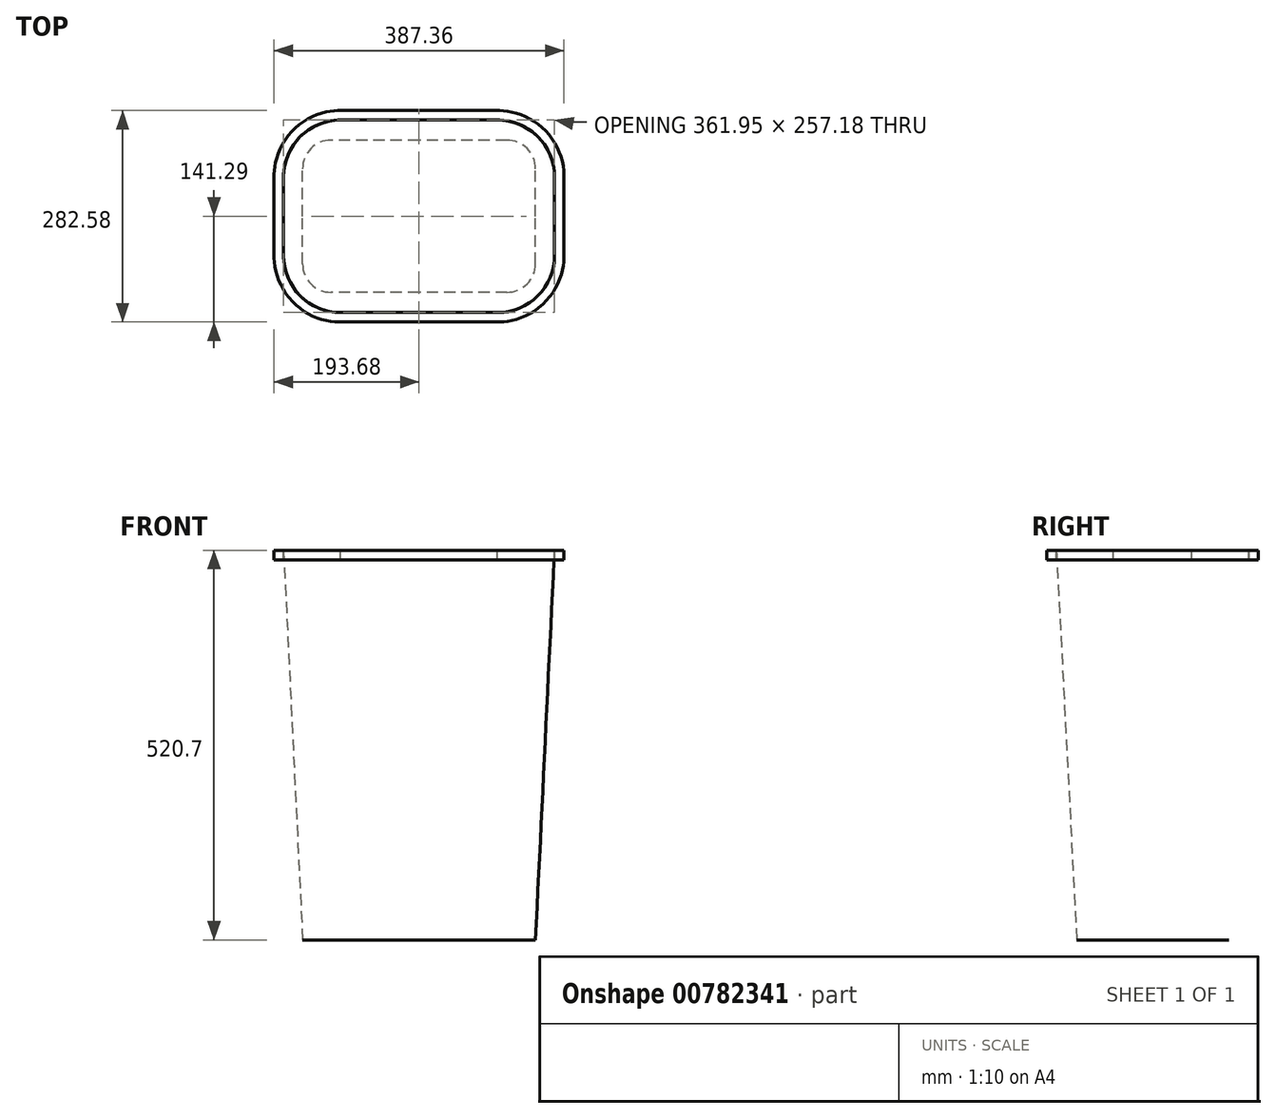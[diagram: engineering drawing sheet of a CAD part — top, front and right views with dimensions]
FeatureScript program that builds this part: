
annotation { "Feature Type Name" : "Feature", "Feature Type Description" : "" }
export const myFeature = defineFeature(function(context is Context, id is Id, definition is map)
    precondition{}
    {
        {
            var Q0;
            Q0=qCreatedBy(makeId("Top.planeOp"),FACE);
            var sketch = newSketch(context, id + "F0", { "sketchPlane" : qUnion([Q0])});
            skLineSegment(sketch, "E0.bottom", {"start": v(104.78, -128.59) * mm, "end": v(-104.78, -128.59) * mm});
            skLineSegment(sketch, "E0.top", {"start": v(104.78, 128.59) * mm, "end": v(-104.78, 128.59) * mm});
            skLineSegment(sketch, "E0.left", {"start": v(180.98, -52.39) * mm, "end": v(180.98, 52.39) * mm});
            skLineSegment(sketch, "E0.right", {"start": v(-180.97, -52.39) * mm, "end": v(-180.97, 52.39) * mm});
            skPoint(sketch, "E0.middle", {"position": v(0, 0) * mm});
            skPoint(sketch, "E1.visualSharp", {"position": v(-180.98, 128.59) * mm});
            skArc(sketch, "E1.filletArc", {"start": v(-104.78, 128.59) * mm, "mid": v(-158.66, 106.27) * mm, "end": v(-180.97, 52.39) * mm});
            skLineSegment(sketch, "E2", {"start": v(-180.97, 0) * mm, "end": v(180.97, 0) * mm, "construction": true});
            skLineSegment(sketch, "E3", {"start": v(0, 128.59) * mm, "end": v(0, -128.59) * mm});
            skArc(sketch, "E4.MirrorCS", {"start": v(-104.78, -128.59) * mm, "mid": v(-158.66, -106.27) * mm, "end": v(-180.97, -52.39) * mm});
            skLineSegment(sketch, "E5.MirrorCS", {"start": v(0, -128.59) * mm, "end": v(0, 128.59) * mm});
            skLineSegment(sketch, "E6.MirrorCS", {"start": v(0, 128.59) * mm, "end": v(0, -128.59) * mm, "construction": true});
            skArc(sketch, "E7.MirrorCS", {"start": v(104.78, 128.59) * mm, "mid": v(158.66, 106.27) * mm, "end": v(180.98, 52.39) * mm});
            skArc(sketch, "E8.MirrorCS", {"start": v(104.78, -128.59) * mm, "mid": v(158.66, -106.27) * mm, "end": v(180.98, -52.39) * mm});
            skPoint(sketch, "E9.orphan", {"position": v(-180.97, -128.59) * mm});
            skPoint(sketch, "E10.orphan", {"position": v(180.98, -128.59) * mm});
            skPoint(sketch, "E11.orphan", {"position": v(180.97, 128.59) * mm});
            skSolve(sketch);
        }
        {
            var Q0;
            {var subQ0=sQuery(id+"F0.wireOp",EDGE,"E1.filletArc");Q0=makeQuery(id+"F0.imprint","IMPRINT",FACE,{"disambiguationData":[TD([[makeQuery(id+"F0.imprint","IMPRINT",EDGE,{"derivedFrom":subQ0}),1.0]])]});}
            cPlane(context, id + "F1", {"entities" : qUnion([Q0]), "cplaneType" : CPlaneType.OFFSET, "offset" : 520.7 * mm, "oppositeDirection" : true, "width" : 152.4 * mm, "height" : 152.4 * mm});
        }
        {
            var Q0;
            Q0=qCreatedBy(id+"F1.planeOp",FACE);
            var sketch = newSketch(context, id + "F2", { "sketchPlane" : qUnion([Q0])});
            skLineSegment(sketch, "E12.0", {"start": v(-180.97, 0) * mm, "end": v(180.97, 0) * mm, "construction": true});
            skLineSegment(sketch, "E13.0", {"start": v(0, 128.59) * mm, "end": v(0, -128.59) * mm, "construction": true});
            skLineSegment(sketch, "E14.bottom", {"start": v(117.48, -101.6) * mm, "end": v(-117.48, -101.6) * mm});
            skLineSegment(sketch, "E14.top", {"start": v(117.47, 101.6) * mm, "end": v(-117.47, 101.6) * mm});
            skLineSegment(sketch, "E14.left", {"start": v(155.58, -63.5) * mm, "end": v(155.58, 63.5) * mm});
            skLineSegment(sketch, "E14.right", {"start": v(-155.57, -63.5) * mm, "end": v(-155.57, 63.5) * mm});
            skPoint(sketch, "E14.middle", {"position": v(0, 0) * mm});
            skPoint(sketch, "E15.visualSharp", {"position": v(-155.57, 101.6) * mm});
            skArc(sketch, "E15.filletArc", {"start": v(-117.48, 101.6) * mm, "mid": v(-144.42, 90.44) * mm, "end": v(-155.57, 63.5) * mm});
            skArc(sketch, "E16.MirrorCS", {"start": v(-117.47, -101.6) * mm, "mid": v(-144.42, -90.44) * mm, "end": v(-155.57, -63.5) * mm});
            skArc(sketch, "E17.MirrorCS", {"start": v(117.47, 101.6) * mm, "mid": v(144.42, 90.44) * mm, "end": v(155.58, 63.5) * mm});
            skArc(sketch, "E18.MirrorCS", {"start": v(117.48, -101.6) * mm, "mid": v(144.42, -90.44) * mm, "end": v(155.58, -63.5) * mm});
            skPoint(sketch, "E19.orphan", {"position": v(-155.57, -101.6) * mm});
            skPoint(sketch, "E20.orphan", {"position": v(155.58, -101.6) * mm});
            skPoint(sketch, "E21.orphan", {"position": v(155.58, 101.6) * mm});
            skPoint(sketch, "E22", {"position": v(-155.57, -25.4) * mm});
            skPoint(sketch, "E23", {"position": v(-155.57, 25.4) * mm});
            skPoint(sketch, "E24", {"position": v(155.58, 25.4) * mm});
            skPoint(sketch, "E25", {"position": v(155.58, -25.4) * mm});
            skPoint(sketch, "E26", {"position": v(0, 101.6) * mm});
            skPoint(sketch, "E27", {"position": v(0, -101.6) * mm});
            skSolve(sketch);
        }
        {
            var Q0;
            Q0=sQuery(id+"F0.wireOp",EDGE,"E0.right");
            cPoint(context, id + "F3", {"entities" : qUnion([Q0]), "parameter" : 0.5});
        }
        {
            var Q0;
            Q0=sQuery(id+"F2.wireOp",VERTEX,"E22");
            var Q1;
            Q1 = qCreatedBy(id + "F3" ,VERTEX);
            var Q2;
            Q2=sQuery(id+"F2.wireOp",VERTEX,"E23");
            cPlane(context, id + "F4", {"entities" : qUnion([Q0, Q1, Q2]), "cplaneType" : CPlaneType.THREE_POINT, "offset" : 25.4 * mm, "width" : 152.4 * mm, "height" : 152.4 * mm});
        }
        {
            var Q0;
            Q0=qCreatedBy(id+"F4.planeOp",FACE);
            var sketch = newSketch(context, id + "F5", { "sketchPlane" : qUnion([Q0])});
            skPoint(sketch, "E28.0", {"position": v(0, 8.82) * mm});
            skPoint(sketch, "E29.0", {"position": v(0, -512.5) * mm});
            skLineSegment(sketch, "E30", {"start": v(0, 8.82) * mm, "end": v(0, -512.5) * mm});
            skSolve(sketch);
        }
        {
            var Q0;
            Q0=sQuery(id+"F0.wireOp",EDGE,"E0.left");
            cPoint(context, id + "F6", {"entities" : qUnion([Q0]), "parameter" : 0.5});
        }
        {
            var Q0;
            Q0=sQuery(id+"F2.wireOp",VERTEX,"E24");
            var Q1;
            Q1=sQuery(id+"F2.wireOp",VERTEX,"E25");
            var Q2;
            Q2 = qCreatedBy(id + "F6" ,VERTEX);
            cPlane(context, id + "F7", {"entities" : qUnion([Q0, Q1, Q2]), "cplaneType" : CPlaneType.THREE_POINT, "offset" : 25.4 * mm, "width" : 152.4 * mm, "height" : 152.4 * mm});
        }
        {
            var Q0;
            Q0=qCreatedBy(id+"F7.planeOp",FACE);
            var sketch = newSketch(context, id + "F8", { "sketchPlane" : qUnion([Q0])});
            skPoint(sketch, "E31.0", {"position": v(0, 8.82) * mm});
            skPoint(sketch, "E32.0", {"position": v(0, -512.5) * mm});
            skLineSegment(sketch, "E33", {"start": v(0, 8.82) * mm, "end": v(0, -512.5) * mm});
            skSolve(sketch);
        }
        {
            var Q0;
            Q0 = qSketchRegion(id + "F0", true);
            var Q1;
            Q1 = qSketchRegion(id + "F2", true);
            var Q2;
            Q2=sQuery(id+"F8.wireOp",EDGE,"E33");
            var Q3;
            Q3=sQuery(id+"F5.wireOp",EDGE,"E30");
            loft(context, id + "F9", {"addGuides" : true, "sheetProfilesArray" : [{ "sheetProfileEntities" : qUnion([Q0]) }, { "sheetProfileEntities" : qUnion([Q1]) }], "guidesArray" : [{ "guideEntities" : qUnion([Q2]), "guideDerivativeType" : LoftGuideDerivativeType.DEFAULT, "guideDerivativeMagnitude" : 1 }, { "guideEntities" : qUnion([Q3]), "guideDerivativeType" : LoftGuideDerivativeType.DEFAULT, "guideDerivativeMagnitude" : 1 }]});
        }
        {
            var Q0;
            Q0=qCreatedBy(makeId("Top.planeOp"),FACE);
            var sketch = newSketch(context, id + "F10", { "sketchPlane" : qUnion([Q0])});
            skFitSpline(sketch, "E34.0", {"points": [v(-104.78, 128.59) * mm, v(-69.85, 128.59) * mm, v(-34.92, 128.59) * mm, v(0, 128.59) * mm]});
            skFitSpline(sketch, "E34.1", {"points": [v(-180.98, 0) * mm, v(-180.98, 17.46) * mm, v(-180.98, 34.93) * mm, v(-180.98, 52.39) * mm]});
            skFitSpline(sketch, "E34.2", {"points": [v(-180.98, 52.39) * mm, v(-180.98, 56.76) * mm, v(-180.4, 63.66) * mm, v(-178.22, 73.13) * mm, v(-175.84, 80.23) * mm, v(-172.7, 87.22) * mm, v(-168.79, 93.97) * mm, v(-164.16, 100.35) * mm, v(-158.87, 106.25) * mm, v(-152.98, 111.58) * mm, v(-146.6, 116.24) * mm, v(-139.85, 120.18) * mm, v(-132.84, 123.37) * mm, v(-125.7, 125.78) * mm, v(-116.17, 128) * mm, v(-109.2, 128.59) * mm, v(-104.78, 128.59) * mm]});
            skFitSpline(sketch, "E34.3", {"points": [v(-180.97, -52.39) * mm, v(-180.97, -34.92) * mm, v(-180.97, -17.46) * mm, v(-180.98, 0) * mm]});
            skFitSpline(sketch, "E34.4", {"points": [v(-104.78, -128.59) * mm, v(-106.28, -128.59) * mm, v(-109.58, -128.5) * mm, v(-115.34, -127.93) * mm, v(-121.74, -126.78) * mm, v(-128.6, -124.9) * mm, v(-135.73, -122.17) * mm, v(-142.9, -118.54) * mm, v(-149.9, -113.99) * mm, v(-156.5, -108.57) * mm, v(-162.51, -102.37) * mm, v(-167.78, -95.53) * mm, v(-172.2, -88.23) * mm, v(-175.69, -80.68) * mm, v(-178.24, -73.1) * mm, v(-179.92, -65.7) * mm, v(-180.81, -58.7) * mm, v(-180.97, -54.41) * mm, v(-180.97, -52.39) * mm]});
            skFitSpline(sketch, "E34.5", {"points": [v(0, -128.59) * mm, v(-34.92, -128.59) * mm, v(-69.85, -128.59) * mm, v(-104.78, -128.59) * mm]});
            skFitSpline(sketch, "E34.6", {"points": [v(104.78, -128.59) * mm, v(69.85, -128.59) * mm, v(34.93, -128.59) * mm, v(0, -128.59) * mm]});
            skFitSpline(sketch, "E34.7", {"points": [v(180.98, -52.39) * mm, v(180.98, -56.76) * mm, v(180.4, -63.66) * mm, v(178.22, -73.13) * mm, v(175.84, -80.23) * mm, v(172.7, -87.22) * mm, v(168.79, -93.97) * mm, v(164.16, -100.35) * mm, v(158.87, -106.25) * mm, v(152.98, -111.58) * mm, v(146.6, -116.24) * mm, v(139.85, -120.18) * mm, v(132.84, -123.37) * mm, v(125.7, -125.78) * mm, v(116.17, -128) * mm, v(109.2, -128.59) * mm, v(104.78, -128.59) * mm]});
            skFitSpline(sketch, "E34.8", {"points": [v(180.98, 0) * mm, v(180.98, -17.46) * mm, v(180.98, -34.92) * mm, v(180.98, -52.39) * mm]});
            skFitSpline(sketch, "E34.9", {"points": [v(180.98, 52.39) * mm, v(180.98, 34.93) * mm, v(180.98, 17.46) * mm, v(180.98, 0) * mm]});
            skFitSpline(sketch, "E34.10", {"points": [v(104.78, 128.59) * mm, v(106.28, 128.59) * mm, v(109.58, 128.5) * mm, v(115.34, 127.93) * mm, v(121.74, 126.78) * mm, v(128.6, 124.9) * mm, v(135.73, 122.17) * mm, v(142.9, 118.54) * mm, v(149.9, 113.99) * mm, v(156.5, 108.57) * mm, v(162.51, 102.37) * mm, v(167.78, 95.53) * mm, v(172.2, 88.23) * mm, v(175.69, 80.68) * mm, v(178.24, 73.1) * mm, v(179.92, 65.7) * mm, v(180.81, 58.7) * mm, v(180.98, 54.41) * mm, v(180.98, 52.39) * mm]});
            skFitSpline(sketch, "E34.11", {"points": [v(0, 128.59) * mm, v(34.93, 128.59) * mm, v(69.85, 128.59) * mm, v(104.78, 128.59) * mm]});
            skFitSpline(sketch, "E35.0", {"points": [v(193.68, 0) * mm, v(193.68, -17.46) * mm, v(193.68, -34.92) * mm, v(193.68, -52.39) * mm]});
            skFitSpline(sketch, "E35.1", {"points": [v(-193.67, -52.39) * mm, v(-193.68, -34.93) * mm, v(-193.68, -17.46) * mm, v(-193.68, 0) * mm]});
            skFitSpline(sketch, "E35.2", {"points": [v(-104.78, -141.29) * mm, v(-106.53, -141.29) * mm, v(-110.39, -141.18) * mm, v(-117.1, -140.53) * mm, v(-124.57, -139.18) * mm, v(-132.57, -136.98) * mm, v(-140.88, -133.8) * mm, v(-149.25, -129.56) * mm, v(-157.4, -124.26) * mm, v(-165.11, -117.93) * mm, v(-172.13, -110.7) * mm, v(-178.29, -102.72) * mm, v(-183.43, -94.2) * mm, v(-187.5, -85.4) * mm, v(-190.49, -76.55) * mm, v(-192.45, -67.92) * mm, v(-193.49, -59.75) * mm, v(-193.67, -54.75) * mm, v(-193.67, -52.39) * mm]});
            skFitSpline(sketch, "E35.3", {"points": [v(0, -141.29) * mm, v(-34.92, -141.29) * mm, v(-69.85, -141.29) * mm, v(-104.78, -141.29) * mm]});
            skFitSpline(sketch, "E35.4", {"points": [v(104.78, -141.29) * mm, v(69.85, -141.29) * mm, v(34.93, -141.29) * mm, v(0, -141.29) * mm]});
            skFitSpline(sketch, "E35.5", {"points": [v(-193.68, 0) * mm, v(-193.68, 17.46) * mm, v(-193.68, 34.93) * mm, v(-193.68, 52.39) * mm]});
            skFitSpline(sketch, "E35.6", {"points": [v(193.68, -52.39) * mm, v(193.68, -54.94) * mm, v(193.5, -58.87) * mm, v(192.91, -64.23) * mm, v(192.05, -69.68) * mm, v(190.46, -76.58) * mm, v(187.68, -84.87) * mm, v(184.01, -93.03) * mm, v(179.46, -100.9) * mm, v(174.06, -108.35) * mm, v(167.88, -115.23) * mm, v(161.02, -121.44) * mm, v(153.58, -126.88) * mm, v(145.7, -131.48) * mm, v(137.52, -135.2) * mm, v(129.19, -138.02) * mm, v(122.24, -139.63) * mm, v(116.75, -140.5) * mm, v(111.33, -141.12) * mm, v(107.36, -141.29) * mm, v(104.78, -141.29) * mm]});
            skFitSpline(sketch, "E35.7", {"points": [v(-193.68, 52.39) * mm, v(-193.68, 54.94) * mm, v(-193.5, 58.87) * mm, v(-192.91, 64.23) * mm, v(-192.05, 69.68) * mm, v(-190.46, 76.58) * mm, v(-187.68, 84.87) * mm, v(-184.01, 93.03) * mm, v(-179.46, 100.9) * mm, v(-174.06, 108.35) * mm, v(-167.88, 115.23) * mm, v(-161.02, 121.44) * mm, v(-153.58, 126.88) * mm, v(-145.7, 131.48) * mm, v(-137.52, 135.2) * mm, v(-129.19, 138.02) * mm, v(-122.24, 139.63) * mm, v(-116.75, 140.5) * mm, v(-111.33, 141.12) * mm, v(-107.36, 141.29) * mm, v(-104.78, 141.29) * mm]});
            skFitSpline(sketch, "E35.8", {"points": [v(-104.78, 141.29) * mm, v(-69.85, 141.29) * mm, v(-34.92, 141.29) * mm, v(0, 141.29) * mm]});
            skFitSpline(sketch, "E35.9", {"points": [v(0, 141.29) * mm, v(34.93, 141.29) * mm, v(69.85, 141.29) * mm, v(104.78, 141.29) * mm]});
            skFitSpline(sketch, "E35.10", {"points": [v(104.78, 141.29) * mm, v(106.53, 141.29) * mm, v(110.39, 141.18) * mm, v(117.1, 140.53) * mm, v(124.57, 139.18) * mm, v(132.57, 136.98) * mm, v(140.88, 133.8) * mm, v(149.25, 129.56) * mm, v(157.4, 124.26) * mm, v(165.11, 117.93) * mm, v(172.13, 110.7) * mm, v(178.29, 102.72) * mm, v(183.43, 94.2) * mm, v(187.5, 85.4) * mm, v(190.49, 76.55) * mm, v(192.45, 67.92) * mm, v(193.49, 59.75) * mm, v(193.68, 54.75) * mm, v(193.68, 52.39) * mm]});
            skFitSpline(sketch, "E35.11", {"points": [v(193.68, 52.39) * mm, v(193.68, 34.93) * mm, v(193.68, 17.46) * mm, v(193.68, 0) * mm]});
            skSolve(sketch);
        }
        {
            var Q0;
            Q0 = qSketchRegion(id + "F10", true);
            extrude(context, id + "F11", {"entities" : qUnion([Q0]), "operationType" : NewBodyOperationType.ADD, "oppositeDirection" : true, "depth" : 12.7 * mm, "offsetDistance" : 25.4 * mm});
        }
        {
            var Q0;
            Q0=makeQuery(id+"F9.opLoft","CAP_FACE",FACE,{"disambiguationData":[OSD([makeQuery(id+"F0.imprint","IMPRINT",FACE,{"disambiguationData":[TD([[makeQuery(id+"F0.imprint","IMPRINT",EDGE,{"derivedFrom":sQuery(id+"F0.wireOp",EDGE,"E0.right")}),-1.0]])]})])],"isStart":true});
            cPlane(context, id + "F12", {"entities" : qUnion([Q0]), "cplaneType" : CPlaneType.OFFSET, "offset" : 203.2 * mm, "oppositeDirection" : true, "width" : 152.4 * mm, "height" : 152.4 * mm});
        }
    });
